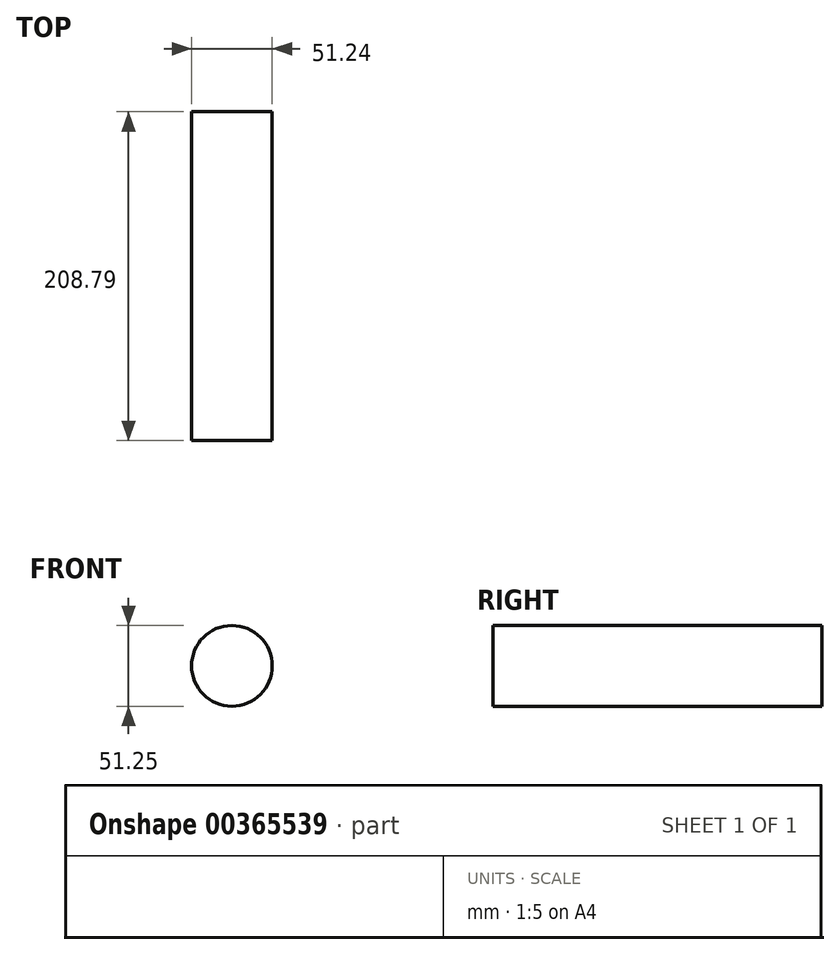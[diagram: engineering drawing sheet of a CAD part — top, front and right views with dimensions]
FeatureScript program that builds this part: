
annotation { "Feature Type Name" : "Feature", "Feature Type Description" : "" }
export const myFeature = defineFeature(function(context is Context, id is Id, definition is map)
    precondition{}
    {
        {
            var Q0;
            Q0=qCreatedBy(makeId("Front.planeOp"),FACE);
            var sketch = newSketch(context, id + "F0", { "sketchPlane" : qUnion([Q0])});
            skCircle(sketch, "E0", {"center": v(41.41, -39.23) * mm, "radius": 25.62 * mm});
            skSolve(sketch);
        }
        {
            var Q0;
            Q0=makeQuery(id+"F0.imprint","IMPRINT",FACE,{"disambiguationData":[TD([[makeQuery(id+"F0.imprint","IMPRINT",EDGE,{"derivedFrom":sQuery(id+"F0.wireOp",EDGE,"E0")}),1.0]])]});
            extrude(context, id + "F1", {"entities" : qUnion([Q0]), "depth" : 208.8 * mm});
        }
    });
